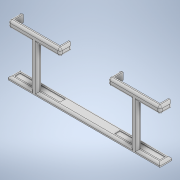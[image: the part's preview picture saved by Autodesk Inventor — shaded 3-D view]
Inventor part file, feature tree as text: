
AUTODESK INVENTOR PART (.ipt)
format: ipt  version: 2020 (Build 240168000, 168)  size: 237,568 bytes
history: native  units: in
note: dims shown in document units (in); Inventor stores cm internally (conversion verified against a paired STEP export)
features: projected_geometry x5, extrude x4, sketch x4, fillet x1
ambient origin geometry x8: Origin, YZ Plane, XZ Plane, XY Plane, X Axis, Y Axis, Z Axis, Center Point
bodies: Solid1 (feature_tree)
feature tree (14):
  extrude  "Extrusion1"  Depth=2.6811in
  extrude  "Extrusion2"  Depth=2.6811in
  extrude  "Extrusion3"  Depth=0.1969in
  extrude  "Extrusion4"  Depth=5.9055in
  fillet  "Fillet1"  Radius=0.0394in
  sketch  "Sketch2"  dims[d0=0.1969in d1=0.0in d6=2.6811in]
  sketch  "Sketch6"  dims[d7=0.315in d8=2.6811in d9=0.315in d10=0.1969in]
  sketch  "Sketch7"  dims[d11=0.1969in d12=0.1969in]
  projected_geometry  "Projected Loop2"
  projected_geometry  "Projected Loop3"
  projected_geometry  "Projected Loop4"
  sketch  "Sketch8"  dims[d13=0.1969in d14=5.9055in d15=0.0394in d16=0.0in d17=0.3937in d19=0.3937in d20=2.4769in d21=0.0in d22=0.1969in d23=0.4144in d24=0.0in d25=0.1969in d26=0.125in]
  projected_geometry  "Projected Loop5"
  projected_geometry  "Projected Loop6"
